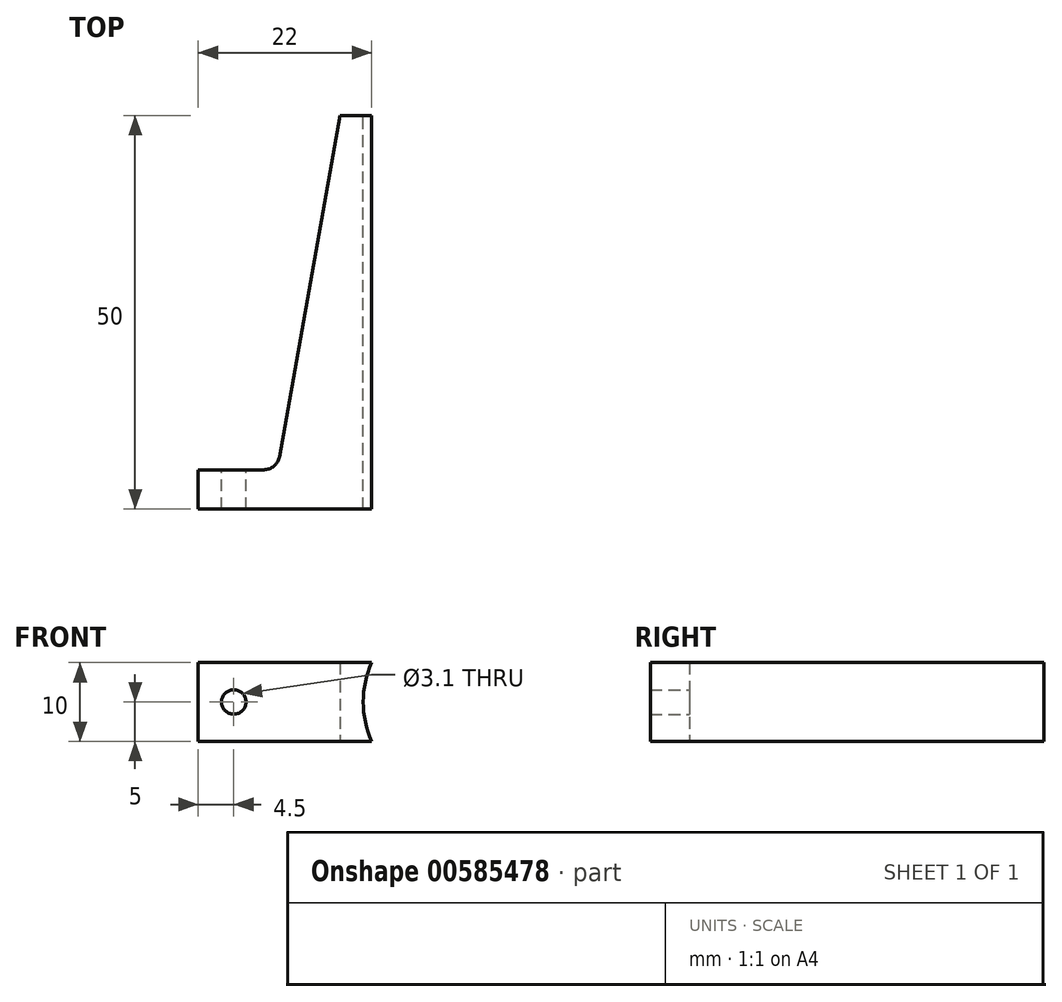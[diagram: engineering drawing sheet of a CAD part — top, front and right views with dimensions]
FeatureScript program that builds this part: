
annotation { "Feature Type Name" : "Feature", "Feature Type Description" : "" }
export const myFeature = defineFeature(function(context is Context, id is Id, definition is map)
    precondition{}
    {
        {
            var Q0;
            Q0=qCreatedBy(makeId("Top.planeOp"),FACE);
            var sketch = newSketch(context, id + "F0", { "sketchPlane" : qUnion([Q0])});
            skLineSegment(sketch, "E0", {"start": v(0, 0) * mm, "end": v(0, 5) * mm});
            skLineSegment(sketch, "E1", {"start": v(0, 5) * mm, "end": v(10, 5) * mm});
            skLineSegment(sketch, "E2", {"start": v(10, 5) * mm, "end": v(18, 50) * mm});
            skLineSegment(sketch, "E3", {"start": v(18, 50) * mm, "end": v(22, 50) * mm});
            skLineSegment(sketch, "E4", {"start": v(22, 50) * mm, "end": v(22, 0) * mm});
            skLineSegment(sketch, "E5", {"start": v(22, 0) * mm, "end": v(0, 0) * mm});
            skSolve(sketch);
        }
        {
            var Q0;
            Q0=makeQuery(id+"F0.imprint","IMPRINT",FACE,{"disambiguationData":[TD([[makeQuery(id+"F0.imprint","IMPRINT",EDGE,{"derivedFrom":sQuery(id+"F0.wireOp",EDGE,"E0")}),-1.0]])]});
            extrude(context, id + "F1", {"entities" : qUnion([Q0]), "depth" : 10 * mm, "offsetDistance" : 25 * mm});
        }
        {
            var Q0;
            Q0=makeQuery(id+"F1.opExtrude","SWEPT_FACE",FACE,{"disambiguationData":[OSD([sQuery(id+"F0.wireOp",EDGE,"E3")])]});
            var sketch = newSketch(context, id + "F2", { "sketchPlane" : qUnion([Q0])});
            skCircle(sketch, "E6", {"center": v(-33.46, 5) * mm, "radius": 12.5 * mm});
            skPoint(sketch, "E6.centerSnap0", {"position": v(-22, 5) * mm});
            skSolve(sketch);
        }
        {
            var Q0;
            {var subQ1=sQuery(id+"F0.wireOp",EDGE,"E3");var subQ2=makeQuery(id+"F1.opExtrude","SWEPT_EDGE",EDGE,{"disambiguationData":[OSD([subQ1,sQuery(id+"F0.wireOp",EDGE,"E4")])]});Q0=makeQuery(id+"F2.imprint","IMPRINT",FACE,{"disambiguationData":[TD([[makeQuery(id+"F2.imprint","IMPRINT",EDGE,{"derivedFrom":subQ2}),-1.0]])]});}
            var Q1;
            {var subQ1=sQuery(id+"F0.wireOp",EDGE,"E3");var subQ2=makeQuery(id+"F1.opExtrude","SWEPT_EDGE",EDGE,{"disambiguationData":[OSD([subQ1,sQuery(id+"F0.wireOp",EDGE,"E4")])]});Q1=makeQuery(id+"F2.imprint","IMPRINT",FACE,{"disambiguationData":[TD([[makeQuery(id+"F2.imprint","IMPRINT",EDGE,{"derivedFrom":subQ2}),1.0]])]});}
            extrude(context, id + "F3", {"entities" : qUnion([Q0, Q1]), "operationType" : NewBodyOperationType.REMOVE, "endBound" : BoundingType.THROUGH_ALL, "oppositeDirection" : true, "depth" : 25 * mm, "offsetDistance" : 25 * mm});
        }
        {
            var Q0;
            Q0=makeQuery(id+"F1.opExtrude","SWEPT_FACE",FACE,{"disambiguationData":[OSD([sQuery(id+"F0.wireOp",EDGE,"E1")])]});
            var sketch = newSketch(context, id + "F4", { "sketchPlane" : qUnion([Q0])});
            skPoint(sketch, "E7", {"position": v(-4.5, 5) * mm});
            skLineSegment(sketch, "E8", {"start": v(0, 5) * mm, "end": v(-4.5, 5) * mm, "construction": true});
            skSolve(sketch);
        }
        {
            var Q0;
            Q0=sQuery(id+"F4.wireOp",VERTEX,"E7");
            var Q1;
            Q1=makeQuery(id+"F1.opExtrude","SWEPT_BODY",BODY,{"disambiguationData":[OSD([sQuery(id+"F0.wireOp",EDGE,"E0"),sQuery(id+"F0.wireOp",EDGE,"E1"),sQuery(id+"F0.wireOp",EDGE,"E2"),sQuery(id+"F0.wireOp",EDGE,"E3"),sQuery(id+"F0.wireOp",EDGE,"E4"),sQuery(id+"F0.wireOp",EDGE,"E5")])]});
            hole(context, id + "F5", {"style" : HoleStyle.SIMPLE, "endStyle" : HoleEndStyle.THROUGH, "holeDiameter" : 3.1 * mm, "majorDiameter" : 5 * mm, "isTappedThrough" : true, "tappedDepth" : 12 * mm, "tapClearance" : 3, "locations" : qUnion([Q0]), "scope" : qUnion([Q1])});
        }
        {
            var Q0;
            Q0=makeQuery(id+"F1.opExtrude","SWEPT_EDGE",EDGE,{"disambiguationData":[OSD([sQuery(id+"F0.wireOp",EDGE,"E1"),sQuery(id+"F0.wireOp",EDGE,"E2")])]});
            fillet(context, id + "F6", {"entities" : qUnion([Q0]), "radius" : 2 * mm, "tangentPropagation" : true, "allowEdgeOverflow" : false});
        }
    });
